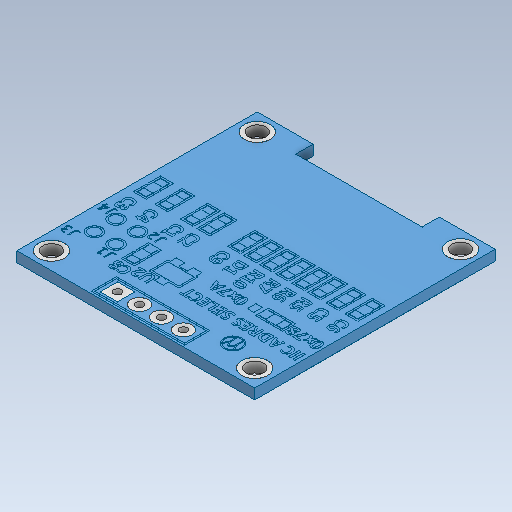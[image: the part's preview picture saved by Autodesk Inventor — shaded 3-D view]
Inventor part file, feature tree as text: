
AUTODESK INVENTOR PART (.ipt)
format: ipt  version: 2020 (Build 240168000, 168)  size: 2,595,328 bytes
history: native  units: mm
features: other x11, hole x7
ambient origin geometry x8: Origin, YZ Plane, XZ Plane, XY Plane, X Axis, Y Axis, Z Axis, Center Point
bodies: Body1 (feature_tree), Body2 (feature_tree), Body3 (feature_tree), Body4 (feature_tree), Body5 (feature_tree), Body6 (feature_tree), Body7 (feature_tree), Body8 (feature_tree), Body9 (feature_tree)
feature tree (18):
  other  "Твердое тело1"
  other  "Твердое тело2"
  other  "Твердое тело3"
  other  "Твердое тело4"
  other  "Твердое тело5"
  other  "Твердое тело6"
  other  "Твердое тело7"
  other  "Твердое тело8"
  other  "Твердое тело9"
  other  "board_body"
  other  "Body 97"
  hole  "hole"  [1 undecoded]
  hole  "hole1"  [1 undecoded]
  hole  "hole3"  [1 undecoded]
  hole  "hole4"  [1 undecoded]
  hole  "hole5"  [1 undecoded]
  hole  "hole6"  [1 undecoded]
  hole  "hole7"  [1 undecoded]
note: 7 required parameter values undecoded (feature->parameter linkage not recoverable at this tier; creation-order binding heuristic only, values carry confidence <= 0.55)
